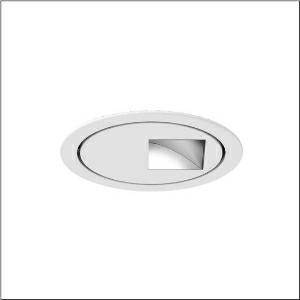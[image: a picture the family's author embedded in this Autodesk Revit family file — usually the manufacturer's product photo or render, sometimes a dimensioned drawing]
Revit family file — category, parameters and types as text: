
# Revit family: lunis_11_mini_round_51dk11b72wg21
name_source: partatom
category: Lighting Fixtures
units: mm (PartAtom-declared; Revit-internal decimal feet)

## family parameters
Cut with Voids When Loaded = No
Host = Face
Light Source = No
Part Type = Normal
Room Calculation Point = No
Round Connector Dimension = Use Diameter
Shared = No

## types (1)
- Lunis 11 mini round (1 x LED 4000K / CRI = 80 (unbekannt), 2470 lm, 4000K)
    Apparent Load = 28 VA
    CIE Flux Codes = 44 77 97 100 100
    Color Rendering = 80
    Color Temperature = 4000K
    Default Elevation = 1800 mm
    Description = Lunis 11 mini round, downlight, light control with wallwasher, of highly reflective aluminium, highly specular, light emission: direct distribution, LED rated luminous flux: 2.470lm, light colour: 840, control gear: ECG, with terminal, 3-pole, mains connection: 220..230V, AC/DC, 0/50..60Hz, LED module, luminaire module, of aluminium, highly specular, white, diameter: 176mm, clamping range: 1..40mm, recessing ring, of plastic, traffic white (RAL 9016), protection rating (complete): IP20, insulation class (complete): insulation class II (safety insulation), certification: CE, permissible ambient temperature for indoor applications: 0..+35°C, packaging unit: 1 piece
    Height = 0 mm  [stored 0 ft]
    Lamp = 1 x LED 4000K / CRI >= 80 (unbekannt)
    Lamp Light Flux = 2470 lm
    Lamp count = 1
    Length = 176 mm
    Luminous efficacy = 88 lm/W
    Manufacturer = Siteco
    ModVariant = No
    Model = 51DK11B72WG21
    Mounting Place = Ceiling
    Mounting Type = Recessed
    Number of Poles = 1
    OnlyDefault = Yes
    Power Factor = 1
    Product Name = Lunis 11 mini round
    Product group = downlight | ceiling recessed
    ProductGroupID = 402
    Protection Class = Protection class II
    Protection Degree = IP 20
    RLX_Detail_Level = 1
    RlxData = <blob elided: 59481 chars, md5=665437ac>
    Socket = socket
    Standby Power = 0 W
    System Light Flux = 2470 lm
    System Power = 28 W
    Type Comments = Product without accessories
    Type Image = l_1004772.jpg
    URL = http://relux.com
    VarID = ---
    Voltage = 0 V
    Weight = 0.00 kg
    Width = 176 mm

note: [stored X ft] marks values corroborated as IEEE doubles in the binary element streams (Revit-internal decimal feet)

## geometry (parser evidence)
native form markers: Blend x4, Sweep x10
no freeform markers — native parametric forms only
